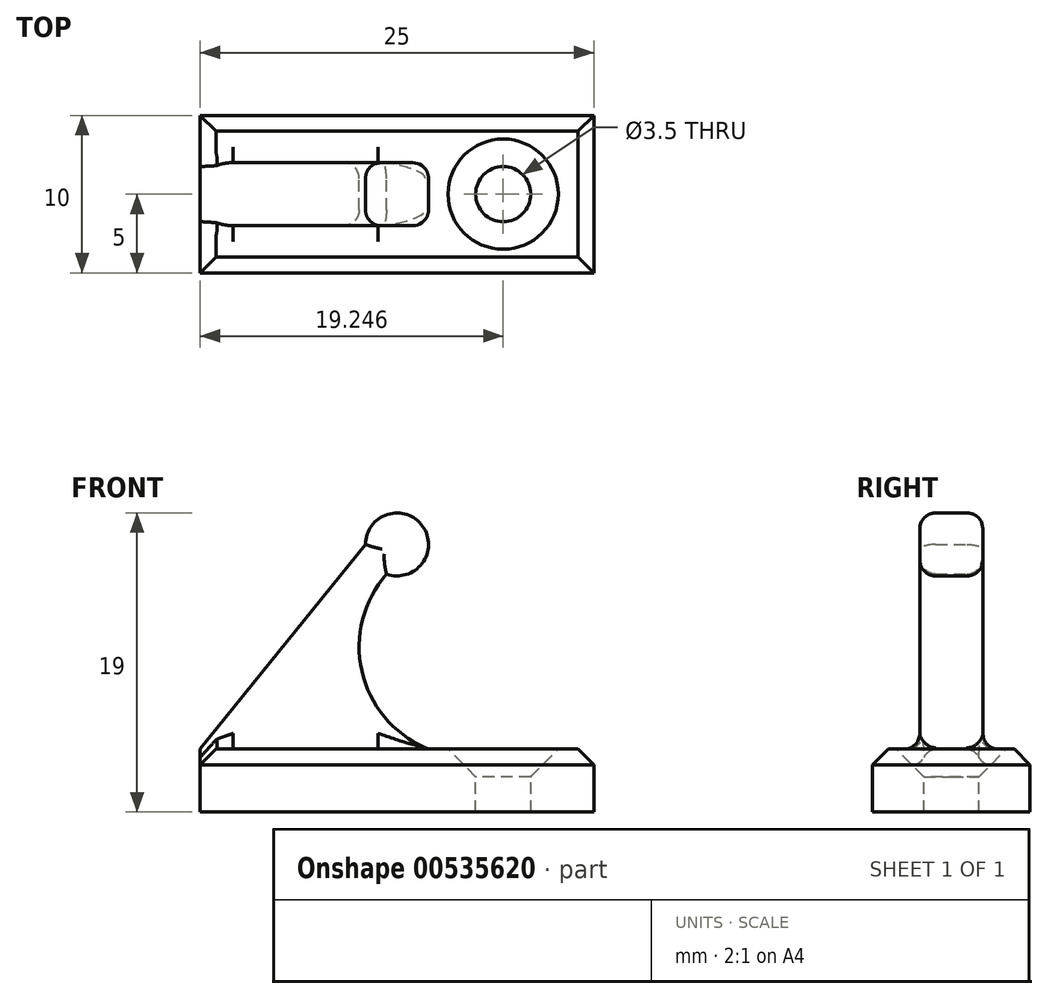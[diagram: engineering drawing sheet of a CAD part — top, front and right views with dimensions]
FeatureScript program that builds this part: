
annotation { "Feature Type Name" : "Feature", "Feature Type Description" : "" }
export const myFeature = defineFeature(function(context is Context, id is Id, definition is map)
    precondition{}
    {
        {
            var Q0;
            Q0=qCreatedBy(makeId("Front.planeOp"),FACE);
            var sketch = newSketch(context, id + "F0", { "sketchPlane" : qUnion([Q0])});
            skLineSegment(sketch, "E0.bottom", {"start": v(12.5, -2) * mm, "end": v(-12.5, -2) * mm});
            skLineSegment(sketch, "E0.top", {"start": v(12.5, 2) * mm, "end": v(-12.5, 2) * mm});
            skLineSegment(sketch, "E0.left", {"start": v(12.5, -2) * mm, "end": v(12.5, 2) * mm});
            skLineSegment(sketch, "E0.right", {"start": v(-12.5, -2) * mm, "end": v(-12.5, 2) * mm});
            skPoint(sketch, "E0.middle", {"position": v(0, 0) * mm});
            skCircle(sketch, "E1", {"center": v(0, 15) * mm, "radius": 2 * mm});
            skLineSegment(sketch, "E2", {"start": v(-6.2, 15) * mm, "end": v(6.4, 15) * mm});
            skPoint(sketch, "E3", {"position": v(-2, 15) * mm});
            skPoint(sketch, "E4", {"position": v(2, 15) * mm});
            skPoint(sketch, "E5", {"position": v(2, 2) * mm});
            skLineSegment(sketch, "E6", {"start": v(-12.5, 2) * mm, "end": v(-2, 15) * mm});
            skArc(sketch, "E7", {"start": v(2, 15) * mm, "mid": v(-2.4, 8.5) * mm, "end": v(2, 2) * mm});
            skSolve(sketch);
        }
        {
            var Q0;
            Q0=makeQuery(id+"F0.imprint","IMPRINT",FACE,{"disambiguationData":[TD([[makeQuery(id+"F0.imprint","IMPRINT",EDGE,{"derivedFrom":sQuery(id+"F0.wireOp",EDGE,"E0.bottom")}),-1.0]])]});
            extrude(context, id + "F1", {"entities" : qUnion([Q0]), "endBound" : BoundingType.SYMMETRIC, "depth" : 10 * mm, "offsetDistance" : 25 * mm});
        }
        {
            var Q0;
            {var subQ0=sQuery(id+"F0.wireOp",EDGE,"E6");Q0=makeQuery(id+"F0.imprint","IMPRINT",FACE,{"disambiguationData":[TD([[makeQuery(id+"F0.imprint","IMPRINT",EDGE,{"derivedFrom":subQ0}),-1.0]])]});}
            extrude(context, id + "F2", {"entities" : qUnion([Q0]), "operationType" : NewBodyOperationType.ADD, "endBound" : BoundingType.SYMMETRIC, "depth" : 4 * mm, "offsetDistance" : 25 * mm});
        }
        {
            var Q0;
            Q0=makeQuery(id+"F1.opExtrude","CAP_EDGE",EDGE,{"disambiguationData":[OSD([sQuery(id+"F0.wireOp",EDGE,"E0.top")])],"isStart":false});
            var Q1;
            Q1=makeQuery(id+"F1.opExtrude","SWEPT_EDGE",EDGE,{"disambiguationData":[OSD([sQuery(id+"F0.wireOp",EDGE,"E0.top"),sQuery(id+"F0.wireOp",EDGE,"E0.left")])]});
            var Q2;
            Q2=makeQuery(id+"F1.opExtrude","CAP_EDGE",EDGE,{"disambiguationData":[OSD([sQuery(id+"F0.wireOp",EDGE,"E0.top")])],"isStart":true});
            var Q3;
            {var subQ0=sQuery(id+"F0.wireOp",EDGE,"E6");var subQ1=sQuery(id+"F0.wireOp",EDGE,"E0.top");var subQ2=sQuery(id+"F0.wireOp",EDGE,"E0.right");Q3=makeQuery(id+"F2.boolean.opBoolean","SPLIT",EDGE,{"disambiguationData":[TD([makeQuery(id+"F1.opExtrude","CAP_FACE",FACE,{"disambiguationData":[OSD([sQuery(id+"F0.wireOp",EDGE,"E0.bottom"),subQ1,sQuery(id+"F0.wireOp",EDGE,"E0.left"),subQ2])],"isStart":true})])],"derivedFrom":makeQuery(id+"F1.opExtrude","SWEPT_EDGE",EDGE,{"disambiguationData":[OSD([subQ1,subQ2,subQ0])]})});}
            var Q4;
            {var subQ0=sQuery(id+"F0.wireOp",EDGE,"E0.right");var subQ1=sQuery(id+"F0.wireOp",EDGE,"E6");var subQ2=sQuery(id+"F0.wireOp",EDGE,"E0.top");Q4=makeQuery(id+"F2.boolean.opBoolean","SPLIT",EDGE,{"disambiguationData":[TD([makeQuery(id+"F1.opExtrude","CAP_FACE",FACE,{"disambiguationData":[OSD([sQuery(id+"F0.wireOp",EDGE,"E0.bottom"),subQ2,sQuery(id+"F0.wireOp",EDGE,"E0.left"),subQ0])],"isStart":false})])],"derivedFrom":makeQuery(id+"F1.opExtrude","SWEPT_EDGE",EDGE,{"disambiguationData":[OSD([subQ2,subQ0,subQ1])]})});}
            chamfer(context, id + "F3", {"entities" : qUnion([Q0, Q1, Q2, Q3, Q4]), "width" : 1 * mm, "tangentPropagation" : true});
        }
        {
            var Q0;
            Q0=makeQuery(id+"F1.opExtrude","SWEPT_FACE",FACE,{"disambiguationData":[OSD([sQuery(id+"F0.wireOp",EDGE,"E0.top")])]});
            var sketch = newSketch(context, id + "F4", { "sketchPlane" : qUnion([Q0])});
            skPoint(sketch, "E8", {"position": v(6.75, 0) * mm});
            skPoint(sketch, "E8.positionSnap0", {"position": v(11.5, 0) * mm});
            skSolve(sketch);
        }
        {
            var Q0;
            Q0=sQuery(id+"F4.wireOp",VERTEX,"E8");
            var Q1;
            Q1=makeQuery(id+"F1.opExtrude","SWEPT_BODY",BODY,{"disambiguationData":[OSD([sQuery(id+"F0.wireOp",EDGE,"E0.bottom"),sQuery(id+"F0.wireOp",EDGE,"E0.top"),sQuery(id+"F0.wireOp",EDGE,"E0.left"),sQuery(id+"F0.wireOp",EDGE,"E0.right")])]});
            hole(context, id + "F5", {"style" : HoleStyle.C_SINK, "endStyle" : HoleEndStyle.BLIND, "holeDiameter" : 3.5 * mm, "cSinkDiameter" : 7 * mm, "cSinkAngle" : 90 * degree, "holeDepth" : 10 * mm, "isTappedThrough" : true, "tappedDepth" : 12 * mm, "tapClearance" : 3, "locations" : qUnion([Q0]), "scope" : qUnion([Q1])});
        }
        {
            var Q0;
            {var subQ0=sQuery(id+"F0.wireOp",EDGE,"E2");var subQ1=sQuery(id+"F0.wireOp",EDGE,"E1");var subQ2=makeQuery(id+"F0.imprint","INTERSECT",VERTEX,{"derivedFrom":[subQ1,subQ0,sQuery(id+"F0.wireOp",EDGE,"E6")]});Q0=makeQuery(id+"F0.imprint","IMPRINT",FACE,{"disambiguationData":[TD([[makeQuery(id+"F0.imprint","IMPRINT",EDGE,{"disambiguationData":[TD([[subQ2,1.0]])],"derivedFrom":subQ1}),1.0]])]});}
            var Q1;
            {var subQ0=sQuery(id+"F0.wireOp",EDGE,"E7");var subQ1=sQuery(id+"F0.wireOp",EDGE,"E1");var subQ3=makeQuery(id+"F0.imprint","INTERSECT",VERTEX,{"derivedFrom":[subQ1,subQ0]});Q1=makeQuery(id+"F0.imprint","IMPRINT",FACE,{"disambiguationData":[TD([[makeQuery(id+"F0.imprint","IMPRINT",EDGE,{"disambiguationData":[TD([[subQ3,-1.0]])],"derivedFrom":subQ1}),1.0]])]});}
            var Q2;
            {var subQ1=sQuery(id+"F0.wireOp",EDGE,"E1");var subQ3=sQuery(id+"F0.wireOp",EDGE,"E7");var subQ4=makeQuery(id+"F0.imprint","INTERSECT",VERTEX,{"derivedFrom":[subQ1,subQ3]});Q2=makeQuery(id+"F0.imprint","IMPRINT",FACE,{"disambiguationData":[TD([[makeQuery(id+"F0.imprint","IMPRINT",EDGE,{"disambiguationData":[TD([[subQ4,1.0]])],"derivedFrom":subQ1}),1.0]])]});}
            extrude(context, id + "F6", {"entities" : qUnion([Q0, Q1, Q2]), "operationType" : NewBodyOperationType.ADD, "endBound" : BoundingType.SYMMETRIC, "depth" : 4 * mm, "offsetDistance" : 25 * mm});
        }
        {
            var Q0;
            Q0=makeQuery(id+"F2.opExtrude","CAP_EDGE",EDGE,{"disambiguationData":[OSD([sQuery(id+"F0.wireOp",EDGE,"E6")])],"isStart":false});
            var Q1;
            Q1=makeQuery(id+"F2.opExtrude","CAP_EDGE",EDGE,{"disambiguationData":[OSD([sQuery(id+"F0.wireOp",EDGE,"E6")])],"isStart":true});
            var Q2;
            Q2=makeQuery(id+"F2.opExtrude","CAP_EDGE",EDGE,{"disambiguationData":[OSD([sQuery(id+"F0.wireOp",EDGE,"E7")])],"isStart":false});
            var Q3;
            Q3=makeQuery(id+"F2.opExtrude","CAP_EDGE",EDGE,{"disambiguationData":[OSD([sQuery(id+"F0.wireOp",EDGE,"E7")])],"isStart":true});
            var Q4;
            Q4=makeQuery(id+"F6.opExtrude","CAP_EDGE",EDGE,{"disambiguationData":[OSD([sQuery(id+"F0.wireOp",EDGE,"E1")])],"isStart":false});
            var Q5;
            Q5=makeQuery(id+"F6.opExtrude","CAP_EDGE",EDGE,{"disambiguationData":[OSD([sQuery(id+"F0.wireOp",EDGE,"E1")])],"isStart":true});
            fillet(context, id + "F7", {"entities" : qUnion([Q0, Q1, Q2, Q3, Q4, Q5]), "radius" : 1 * mm, "tangentPropagation" : true, "allowEdgeOverflow" : false});
        }
        {
            var Q0;
            Q0=makeQuery(id+"F2.opExtrude","CAP_EDGE",EDGE,{"disambiguationData":[OSD([sQuery(id+"F0.wireOp",EDGE,"E0.top")])],"isStart":true});
            var Q1;
            Q1=makeQuery(id+"F2.opExtrude","CAP_EDGE",EDGE,{"disambiguationData":[OSD([sQuery(id+"F0.wireOp",EDGE,"E0.top")])],"isStart":false});
            var Q2;
            Q2=makeQuery(id+"F7.opFillet","BLEND_EDGE",EDGE,{"blendedFrom":[makeQuery(id+"F2.opExtrude","CAP_EDGE",EDGE,{"disambiguationData":[OSD([sQuery(id+"F0.wireOp",EDGE,"E7")])],"isStart":false}),makeQuery(id+"F1.opExtrude","SWEPT_FACE",FACE,{"disambiguationData":[OSD([sQuery(id+"F0.wireOp",EDGE,"E0.top")])]})],"blendedInto":[makeQuery(id+"F1.opExtrude","SWEPT_FACE",FACE,{"disambiguationData":[OSD([sQuery(id+"F0.wireOp",EDGE,"E0.top")])]})]});
            var Q3;
            Q3=makeQuery(id+"F2.opExtrude","SWEPT_EDGE",EDGE,{"disambiguationData":[OSD([sQuery(id+"F0.wireOp",EDGE,"E0.top"),sQuery(id+"F0.wireOp",EDGE,"E7")])]});
            var Q4;
            Q4=makeQuery(id+"F7.opFillet","BLEND_EDGE",EDGE,{"blendedFrom":[makeQuery(id+"F2.opExtrude","CAP_EDGE",EDGE,{"disambiguationData":[OSD([sQuery(id+"F0.wireOp",EDGE,"E7")])],"isStart":true}),makeQuery(id+"F1.opExtrude","SWEPT_FACE",FACE,{"disambiguationData":[OSD([sQuery(id+"F0.wireOp",EDGE,"E0.top")])]})],"blendedInto":[makeQuery(id+"F1.opExtrude","SWEPT_FACE",FACE,{"disambiguationData":[OSD([sQuery(id+"F0.wireOp",EDGE,"E0.top")])]})]});
            var Q5;
            {var subQ0=sQuery(id+"F0.wireOp",EDGE,"E0.right");var subQ1=sQuery(id+"F0.wireOp",EDGE,"E6");var subQ2=sQuery(id+"F0.wireOp",EDGE,"E0.top");Q5=makeQuery(id+"F7.opFillet","BLEND_EDGE",EDGE,{"blendedFrom":[makeQuery(id+"F2.opExtrude","CAP_EDGE",EDGE,{"disambiguationData":[OSD([subQ1])],"isStart":false}),makeQuery(id+"F3.opChamfer","BLEND_FACE",FACE,{"disambiguationData":[OSD([subQ2,subQ0,subQ1]),TDD([makeQuery(id+"F2.boolean.opBoolean","SPLIT",EDGE,{"disambiguationData":[TD([makeQuery(id+"F1.opExtrude","CAP_FACE",FACE,{"disambiguationData":[OSD([sQuery(id+"F0.wireOp",EDGE,"E0.bottom"),subQ2,sQuery(id+"F0.wireOp",EDGE,"E0.left"),subQ0])],"isStart":false})])],"derivedFrom":makeQuery(id+"F1.opExtrude","SWEPT_EDGE",EDGE,{"disambiguationData":[OSD([subQ2,subQ0,subQ1])]})})])]})],"blendedInto":[makeQuery(id+"F3.opChamfer","BLEND_FACE",FACE,{"disambiguationData":[OSD([subQ2,subQ0,subQ1]),TDD([makeQuery(id+"F2.boolean.opBoolean","SPLIT",EDGE,{"disambiguationData":[TD([makeQuery(id+"F1.opExtrude","CAP_FACE",FACE,{"disambiguationData":[OSD([sQuery(id+"F0.wireOp",EDGE,"E0.bottom"),subQ2,sQuery(id+"F0.wireOp",EDGE,"E0.left"),subQ0])],"isStart":false})])],"derivedFrom":makeQuery(id+"F1.opExtrude","SWEPT_EDGE",EDGE,{"disambiguationData":[OSD([subQ2,subQ0,subQ1])]})})])]})]});}
            var Q6;
            {var subQ0=sQuery(id+"F0.wireOp",EDGE,"E6");var subQ1=sQuery(id+"F0.wireOp",EDGE,"E0.top");var subQ2=sQuery(id+"F0.wireOp",EDGE,"E0.right");Q6=makeQuery(id+"F7.opFillet","BLEND_EDGE",EDGE,{"blendedFrom":[makeQuery(id+"F2.opExtrude","CAP_EDGE",EDGE,{"disambiguationData":[OSD([subQ0])],"isStart":true}),makeQuery(id+"F3.opChamfer","BLEND_FACE",FACE,{"disambiguationData":[OSD([subQ1,subQ2,subQ0]),TDD([makeQuery(id+"F2.boolean.opBoolean","SPLIT",EDGE,{"disambiguationData":[TD([makeQuery(id+"F1.opExtrude","CAP_FACE",FACE,{"disambiguationData":[OSD([sQuery(id+"F0.wireOp",EDGE,"E0.bottom"),subQ1,sQuery(id+"F0.wireOp",EDGE,"E0.left"),subQ2])],"isStart":true})])],"derivedFrom":makeQuery(id+"F1.opExtrude","SWEPT_EDGE",EDGE,{"disambiguationData":[OSD([subQ1,subQ2,subQ0])]})})])]})],"blendedInto":[makeQuery(id+"F3.opChamfer","BLEND_FACE",FACE,{"disambiguationData":[OSD([subQ1,subQ2,subQ0]),TDD([makeQuery(id+"F2.boolean.opBoolean","SPLIT",EDGE,{"disambiguationData":[TD([makeQuery(id+"F1.opExtrude","CAP_FACE",FACE,{"disambiguationData":[OSD([sQuery(id+"F0.wireOp",EDGE,"E0.bottom"),subQ1,sQuery(id+"F0.wireOp",EDGE,"E0.left"),subQ2])],"isStart":true})])],"derivedFrom":makeQuery(id+"F1.opExtrude","SWEPT_EDGE",EDGE,{"disambiguationData":[OSD([subQ1,subQ2,subQ0])]})})])]})]});}
            var Q7;
            Q7=makeQuery(id+"F7.opFillet","BLEND_EDGE",EDGE,{"blendedFrom":[makeQuery(id+"F2.opExtrude","CAP_EDGE",EDGE,{"disambiguationData":[OSD([sQuery(id+"F0.wireOp",EDGE,"E6")])],"isStart":false}),makeQuery(id+"F1.opExtrude","SWEPT_FACE",FACE,{"disambiguationData":[OSD([sQuery(id+"F0.wireOp",EDGE,"E0.top")])]})],"blendedInto":[makeQuery(id+"F1.opExtrude","SWEPT_FACE",FACE,{"disambiguationData":[OSD([sQuery(id+"F0.wireOp",EDGE,"E0.top")])]})]});
            var Q8;
            Q8=makeQuery(id+"F7.opFillet","BLEND_EDGE",EDGE,{"blendedFrom":[makeQuery(id+"F2.opExtrude","CAP_EDGE",EDGE,{"disambiguationData":[OSD([sQuery(id+"F0.wireOp",EDGE,"E6")])],"isStart":true}),makeQuery(id+"F1.opExtrude","SWEPT_FACE",FACE,{"disambiguationData":[OSD([sQuery(id+"F0.wireOp",EDGE,"E0.top")])]})],"blendedInto":[makeQuery(id+"F1.opExtrude","SWEPT_FACE",FACE,{"disambiguationData":[OSD([sQuery(id+"F0.wireOp",EDGE,"E0.top")])]})]});
            fillet(context, id + "F8", {"entities" : qUnion([Q0, Q1, Q2, Q3, Q4, Q5, Q6, Q7, Q8]), "radius" : 1 * mm, "tangentPropagation" : true, "allowEdgeOverflow" : false});
        }
    });
